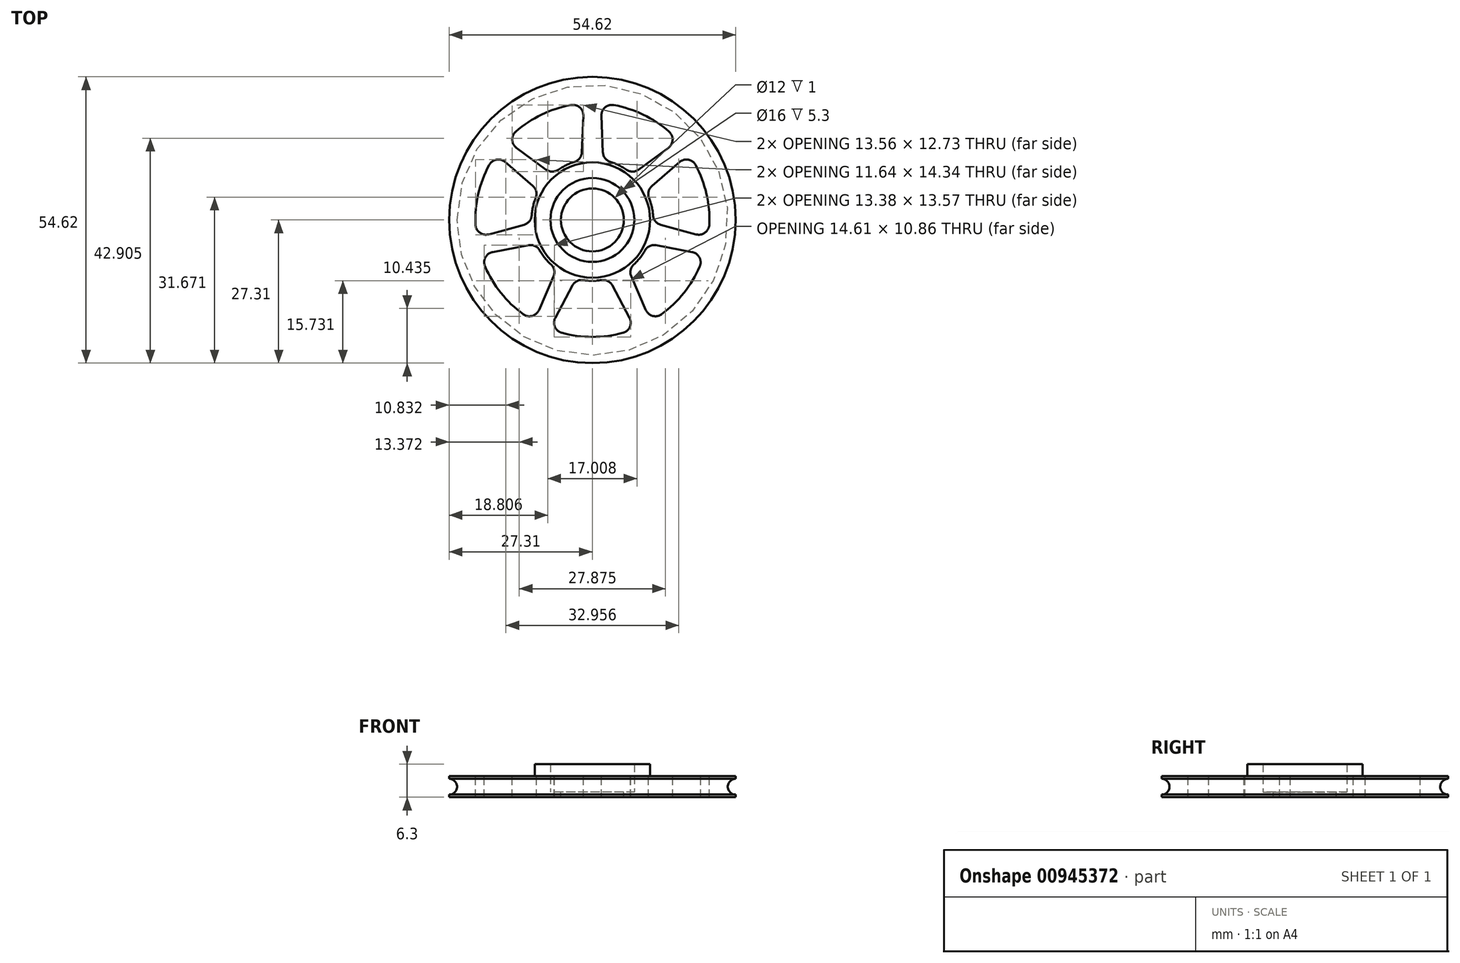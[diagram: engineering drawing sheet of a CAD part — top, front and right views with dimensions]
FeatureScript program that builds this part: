
annotation { "Feature Type Name" : "Feature", "Feature Type Description" : "" }
export const myFeature = defineFeature(function(context is Context, id is Id, definition is map)
    precondition{}
    {
        {
            var Q0;
            Q0=qCreatedBy(makeId("Top.planeOp"),FACE);
            var sketch = newSketch(context, id + "F0", { "sketchPlane" : qUnion([Q0])});
            skCircle(sketch, "E0", {"center": v(0, 0) * mm, "radius": 27.3 * mm});
            skSolve(sketch);
        }
        {
            var Q0;
            Q0=makeQuery(id+"F0.imprint","IMPRINT",FACE,{"disambiguationData":[TD([[makeQuery(id+"F0.imprint","IMPRINT",EDGE,{"derivedFrom":sQuery(id+"F0.wireOp",EDGE,"E0")}),1.0]])]});
            extrude(context, id + "F1", {"entities" : qUnion([Q0]), "depth" : 4 * mm, "offsetDistance" : 25.4 * mm});
        }
        {
            var Q0;
            Q0=makeQuery(id+"F1.opExtrude","CAP_FACE",FACE,{"disambiguationData":[OSD([sQuery(id+"F0.wireOp",EDGE,"E0"),sQuery(id+"F0.wireOp",EDGE,"n39IqKt5-bk1q-LU1x-fgod-8OyBNiFTd7FZ")])],"isStart":false});
            var sketch = newSketch(context, id + "F2", { "sketchPlane" : qUnion([Q0])});
            skCircle(sketch, "E1", {"center": v(0, 0) * mm, "radius": 8 * mm});
            skCircle(sketch, "E2.0", {"center": v(0, 0) * mm, "radius": 11 * mm});
            skSolve(sketch);
        }
        {
            var Q0;
            Q0=qSketchRegion(id+"F2",true);
            extrude(context, id + "F3", {"entities" : qUnion([Q0]), "operationType" : NewBodyOperationType.ADD, "flatOperationType" : FlatOperationType.REMOVE, "depth" : 2.3 * mm, "offsetDistance" : 25.4 * mm, "domain" : OperationDomain.MODEL});
        }
        {
            var Q0;
            Q0=makeQuery(id+"F3.boolean.opBoolean","SPLIT",FACE,{"disambiguationData":[TD([makeQuery(id+"F3.opExtrude","SWEPT_FACE",FACE,{"disambiguationData":[OSD([sQuery(id+"F2.wireOp",EDGE,"E1")])]})])],"derivedFrom":makeQuery(id+"F1.opExtrude","CAP_FACE",FACE,{"disambiguationData":[OSD([sQuery(id+"F0.wireOp",EDGE,"E0")])],"isStart":false})});
            var sketch = newSketch(context, id + "F4", { "sketchPlane" : qUnion([Q0])});
            skCircle(sketch, "E3", {"center": v(0, 0) * mm, "radius": 6 * mm});
            skSolve(sketch);
        }
        {
            var Q0;
            Q0=makeQuery(id+"F4.imprint","IMPRINT",FACE,{"disambiguationData":[TD([[makeQuery(id+"F4.imprint","IMPRINT",EDGE,{"derivedFrom":sQuery(id+"F4.wireOp",EDGE,"E3")}),1.0]])]});
            var Q1;
            Q1=makeQuery(id+"F4.imprint","IMPRINT",FACE,{"disambiguationData":[TD([[makeQuery(id+"F4.imprint","IMPRINT",EDGE,{"derivedFrom":makeQuery(id+"FgYK8jIepfClWtA_1.opExtrude","CAP_EDGE",EDGE,{"disambiguationData":[OSD([sQuery(id+"F8DXjnVyigKkjng_1.wireOp",EDGE,"EUjAMsCd-Zx2B-3j4q-cP5o-T3GrjTijNDqK")])],"isStart":false})}),1.0]])]});
            extrude(context, id + "F5", {"entities" : qUnion([Q0, Q1]), "operationType" : NewBodyOperationType.REMOVE, "oppositeDirection" : true, "depth" : 9 * mm, "offsetDistance" : 25.4 * mm});
        }
        {
            var Q0;
            Q0=qCreatedBy(makeId("Front.planeOp"),FACE);
            var sketch = newSketch(context, id + "F6", { "sketchPlane" : qUnion([Q0])});
            skCircle(sketch, "E4", {"center": v(-27.3, 2) * mm, "radius": 1.5 * mm});
            skLineSegment(sketch, "E5.bottom", {"start": v(-25.8, 0.65) * mm, "end": v(-27.95, 0.65) * mm});
            skLineSegment(sketch, "E5.top", {"start": v(-25.8, 3.35) * mm, "end": v(-27.95, 3.35) * mm});
            skLineSegment(sketch, "E5.left", {"start": v(-25.8, 0.65) * mm, "end": v(-25.8, 3.35) * mm});
            skLineSegment(sketch, "E5.right", {"start": v(-28.8, 1.91) * mm, "end": v(-28.8, 2.09) * mm});
            skLineSegment(sketch, "E6", {"start": v(0, 19.1) * mm, "end": v(0, -12.61) * mm, "construction": true});
            skLineSegment(sketch, "E7", {"start": v(-25.8, 1.83) * mm, "end": v(-25.81, 1.83) * mm});
            skPoint(sketch, "E8.orphan", {"position": v(-38.97, 3.35) * mm});
            skPoint(sketch, "E9.end.orphan", {"position": v(-15.64, 0.65) * mm});
            skPoint(sketch, "E9.start.orphan", {"position": v(-25.8, 2) * mm});
            skSolve(sketch);
        }
        {
            var Q0;
            {var subQ0=sQuery(id+"F6.wireOp",EDGE,"E5.top");var subQ1=sQuery(id+"F6.wireOp",EDGE,"E4");var subQ2=makeQuery(id+"F6.imprint","INTERSECT",VERTEX,{"disambiguationData":[OD(0.0)],"derivedFrom":[subQ1,subQ0]});Q0=makeQuery(id+"F6.imprint","IMPRINT",FACE,{"disambiguationData":[TD([[makeQuery(id+"F6.imprint","IMPRINT",EDGE,{"disambiguationData":[TD([[subQ2,1.0]])],"derivedFrom":subQ1}),1.0]])]});}
            var Q1;
            {var subQ0=sQuery(id+"F6.wireOp",EDGE,"E5.bottom");var subQ1=sQuery(id+"F6.wireOp",EDGE,"E4");var subQ2=makeQuery(id+"F6.imprint","INTERSECT",VERTEX,{"disambiguationData":[OD(0.0)],"derivedFrom":[subQ1,subQ0]});Q1=makeQuery(id+"F6.imprint","IMPRINT",FACE,{"disambiguationData":[TD([[makeQuery(id+"F6.imprint","IMPRINT",EDGE,{"disambiguationData":[TD([[subQ2,-1.0]])],"derivedFrom":subQ1}),1.0]])]});}
            var Q2;
            {var subQ4=sQuery(id+"F6.wireOp",EDGE,"E5.right");Q2=makeQuery(id+"F6.imprint","IMPRINT",FACE,{"disambiguationData":[TD([[makeQuery(id+"F6.imprint","IMPRINT",EDGE,{"derivedFrom":subQ4}),-1.0]])]});}
            var Q3;
            {var subQ0=sQuery(id+"F6.wireOp",EDGE,"p3G3spWP-JurA-dj01-Cwvm-HHlCDoPDIoxd");Q3=makeQuery(id+"F6.imprint","IMPRINT",FACE,{"disambiguationData":[TD([[makeQuery(id+"F6.imprint","IMPRINT",EDGE,{"derivedFrom":subQ0}),1.0]])]});}
            var Q4;
            Q4=makeQuery(id+"F6.imprint","IMPRINT",FACE,{"disambiguationData":[TD([[makeQuery(id+"F6.imprint","IMPRINT",EDGE,{"derivedFrom":sQuery(id+"F6.wireOp",EDGE,"p3G3spWP-JurA-dj01-Cwvm-HHlCDoPDIoxd")}),-1.0]])]});
            var Q5;
            {var subQ0=sQuery(id+"F6.wireOp",EDGE,"E9");Q5=makeQuery(id+"F6.imprint","IMPRINT",FACE,{"disambiguationData":[TD([[makeQuery(id+"F6.imprint","IMPRINT",EDGE,{"derivedFrom":subQ0}),1.0]])]});}
            var Q6;
            Q6=sQuery(id+"F6.wireOp",EDGE,"E6");
            revolve(context, id + "F7", {"operationType" : NewBodyOperationType.REMOVE, "surfaceOperationType" : NewSurfaceOperationType.NEW, "entities" : qUnion([Q0, Q1, Q2, Q3, Q4, Q5]), "axis" : qUnion([Q6]), "revolveType" : RevolveType.FULL, "oppositeDirection" : true});
        }
        {
            var Q0;
            Q0=makeQuery(id+"F3.boolean.opBoolean","SPLIT",FACE,{"disambiguationData":[TD([makeQuery(id+"F3.opExtrude","SWEPT_FACE",FACE,{"disambiguationData":[OSD([sQuery(id+"F2.wireOp",EDGE,"E1")])]})])],"derivedFrom":makeQuery(id+"F1.opExtrude","CAP_FACE",FACE,{"disambiguationData":[OSD([sQuery(id+"F0.wireOp",EDGE,"E0")])],"isStart":false})});
            extrude(context, id + "F8", {"entities" : qUnion([Q0]), "operationType" : NewBodyOperationType.REMOVE, "oppositeDirection" : true, "depth" : 3 * mm, "offsetDistance" : 25 * mm});
        }
        {
            var Q0;
            {var subQ0=sQuery(id+"F0.wireOp",EDGE,"E0");var subQ1=makeQuery(id+"F1.opExtrude","SWEPT_FACE",FACE,{"disambiguationData":[OSD([subQ0])]});Q0=makeQuery(id+"FvaswZWDLJZ7FP9_1.boolean.opBoolean","SPLIT",FACE,{"disambiguationData":[TD([subQ1])],"derivedFrom":makeQuery(id+"F3.boolean.opBoolean","SPLIT",FACE,{"disambiguationData":[TD([subQ1])],"derivedFrom":makeQuery(id+"F1.opExtrude","CAP_FACE",FACE,{"disambiguationData":[OSD([subQ0])],"isStart":false})})});}
            var sketch = newSketch(context, id + "F9", { "sketchPlane" : qUnion([Q0])});
            skArc(sketch, "E10", {"start": v(-4.1, 21.93) * mm, "mid": v(-9.68, 20.1) * mm, "end": v(-14.6, 16.87) * mm});
            skArc(sketch, "E11", {"start": v(-3.41, 11.08) * mm, "mid": v(-5.03, 10.45) * mm, "end": v(-6.54, 9.58) * mm});
            skLineSegment(sketch, "E12.0", {"start": v(-1.73, 19.88) * mm, "end": v(-2, 12.92) * mm});
            skLineSegment(sketch, "E13.0", {"start": v(1.73, 19.88) * mm, "end": v(2, 12.92) * mm});
            skPoint(sketch, "E14.start.orphan", {"position": v(0, 24.6) * mm});
            skPoint(sketch, "E15.visualSharp", {"position": v(-1.63, 22.25) * mm});
            skArc(sketch, "E15.filletArc", {"start": v(-1.73, 19.88) * mm, "mid": v(-2.42, 21.47) * mm, "end": v(-4.1, 21.93) * mm});
            skPoint(sketch, "E16.visualSharp", {"position": v(1.63, 22.25) * mm});
            skArc(sketch, "E16.filletArc", {"start": v(4.1, 21.93) * mm, "mid": v(2.42, 21.47) * mm, "end": v(1.73, 19.88) * mm});
            skPoint(sketch, "E17.visualSharp", {"position": v(-2.06, 11.41) * mm});
            skArc(sketch, "E17.filletArc", {"start": v(-3.41, 11.08) * mm, "mid": v(-2.41, 11.78) * mm, "end": v(-2, 12.92) * mm});
            skPoint(sketch, "E18.visualSharp", {"position": v(2.06, 11.41) * mm});
            skArc(sketch, "E18.filletArc", {"start": v(2, 12.92) * mm, "mid": v(2.41, 11.78) * mm, "end": v(3.41, 11.08) * mm});
            skArc(sketch, "E19.1.0", {"start": v(-16.62, 11.05) * mm, "mid": v(-18.3, 11.5) * mm, "end": v(-19.7, 10.47) * mm});
            skArc(sketch, "E19.1.1", {"start": v(-14.6, 16.87) * mm, "mid": v(-15.28, 15.28) * mm, "end": v(-14.47, 13.75) * mm});
            skLineSegment(sketch, "E19.1.2", {"start": v(-14.47, 13.75) * mm, "end": v(-8.85, 9.62) * mm});
            skLineSegment(sketch, "E19.1.3", {"start": v(-16.62, 11.05) * mm, "end": v(-11.35, 6.49) * mm});
            skArc(sketch, "E19.1.4", {"start": v(-10.8, 4.24) * mm, "mid": v(-10.71, 5.45) * mm, "end": v(-11.35, 6.49) * mm});
            skArc(sketch, "E19.1.5", {"start": v(-8.85, 9.62) * mm, "mid": v(-7.7, 9.23) * mm, "end": v(-6.54, 9.58) * mm});
            skArc(sketch, "E19.2.0", {"start": v(-19, -6.1) * mm, "mid": v(-20.4, -7.13) * mm, "end": v(-20.47, -8.87) * mm});
            skArc(sketch, "E19.2.1", {"start": v(-22.29, -0.89) * mm, "mid": v(-21.47, -2.42) * mm, "end": v(-19.77, -2.74) * mm});
            skLineSegment(sketch, "E19.2.2", {"start": v(-19.77, -2.74) * mm, "end": v(-13.04, -0.92) * mm});
            skLineSegment(sketch, "E19.2.3", {"start": v(-19, -6.1) * mm, "end": v(-12.15, -4.83) * mm});
            skArc(sketch, "E19.2.4", {"start": v(-10.05, -5.8) * mm, "mid": v(-10.94, -4.97) * mm, "end": v(-12.15, -4.83) * mm});
            skArc(sketch, "E19.2.5", {"start": v(-13.04, -0.92) * mm, "mid": v(-12.02, -0.27) * mm, "end": v(-11.57, 0.86) * mm});
            skArc(sketch, "E19.3.0", {"start": v(-7.07, -18.66) * mm, "mid": v(-7.14, -20.4) * mm, "end": v(-5.83, -21.53) * mm});
            skArc(sketch, "E19.3.1", {"start": v(-13.2, -17.98) * mm, "mid": v(-11.5, -18.3) * mm, "end": v(-10.18, -17.16) * mm});
            skLineSegment(sketch, "E19.3.2", {"start": v(-10.18, -17.16) * mm, "end": v(-7.4, -10.77) * mm});
            skLineSegment(sketch, "E19.3.3", {"start": v(-7.07, -18.66) * mm, "end": v(-3.8, -12.5) * mm});
            skArc(sketch, "E19.3.4", {"start": v(-1.74, -11.47) * mm, "mid": v(-2.93, -11.66) * mm, "end": v(-3.8, -12.5) * mm});
            skArc(sketch, "E19.3.5", {"start": v(-7.4, -10.77) * mm, "mid": v(-7.29, -9.56) * mm, "end": v(-7.88, -8.5) * mm});
            skArc(sketch, "E19.4.0", {"start": v(10.18, -17.16) * mm, "mid": v(11.5, -18.3) * mm, "end": v(13.2, -17.98) * mm});
            skArc(sketch, "E19.4.1", {"start": v(5.83, -21.53) * mm, "mid": v(7.14, -20.4) * mm, "end": v(7.07, -18.66) * mm});
            skLineSegment(sketch, "E19.4.2", {"start": v(7.07, -18.66) * mm, "end": v(3.8, -12.5) * mm});
            skLineSegment(sketch, "E19.4.3", {"start": v(10.18, -17.16) * mm, "end": v(7.4, -10.77) * mm});
            skArc(sketch, "E19.4.4", {"start": v(7.88, -8.5) * mm, "mid": v(7.29, -9.56) * mm, "end": v(7.4, -10.77) * mm});
            skArc(sketch, "E19.4.5", {"start": v(3.8, -12.5) * mm, "mid": v(2.93, -11.66) * mm, "end": v(1.74, -11.47) * mm});
            skArc(sketch, "E19.5.0", {"start": v(19.77, -2.74) * mm, "mid": v(21.47, -2.42) * mm, "end": v(22.29, -0.89) * mm});
            skArc(sketch, "E19.5.1", {"start": v(20.47, -8.87) * mm, "mid": v(20.4, -7.13) * mm, "end": v(19, -6.1) * mm});
            skLineSegment(sketch, "E19.5.2", {"start": v(19, -6.1) * mm, "end": v(12.15, -4.83) * mm});
            skLineSegment(sketch, "E19.5.3", {"start": v(19.77, -2.74) * mm, "end": v(13.04, -0.92) * mm});
            skArc(sketch, "E19.5.4", {"start": v(11.57, 0.86) * mm, "mid": v(12.02, -0.27) * mm, "end": v(13.04, -0.92) * mm});
            skArc(sketch, "E19.5.5", {"start": v(12.15, -4.83) * mm, "mid": v(10.94, -4.97) * mm, "end": v(10.05, -5.8) * mm});
            skArc(sketch, "E19.6.0", {"start": v(14.47, 13.75) * mm, "mid": v(15.28, 15.28) * mm, "end": v(14.6, 16.87) * mm});
            skArc(sketch, "E19.6.1", {"start": v(19.7, 10.47) * mm, "mid": v(18.3, 11.5) * mm, "end": v(16.62, 11.05) * mm});
            skLineSegment(sketch, "E19.6.2", {"start": v(16.62, 11.05) * mm, "end": v(11.35, 6.49) * mm});
            skLineSegment(sketch, "E19.6.3", {"start": v(14.47, 13.75) * mm, "end": v(8.85, 9.62) * mm});
            skArc(sketch, "E19.6.4", {"start": v(6.54, 9.58) * mm, "mid": v(7.7, 9.23) * mm, "end": v(8.85, 9.62) * mm});
            skArc(sketch, "E19.6.5", {"start": v(11.35, 6.49) * mm, "mid": v(10.71, 5.45) * mm, "end": v(10.8, 4.24) * mm});
            skArc(sketch, "E20.trimOffspring", {"start": v(-19.7, 10.47) * mm, "mid": v(-21.75, 4.96) * mm, "end": v(-22.29, -0.89) * mm});
            skArc(sketch, "E21.trimOffspring", {"start": v(-10.8, 4.24) * mm, "mid": v(-11.3, 2.58) * mm, "end": v(-11.57, 0.86) * mm});
            skArc(sketch, "E22.trimOffspring", {"start": v(-10.05, -5.8) * mm, "mid": v(-9.07, -7.23) * mm, "end": v(-7.88, -8.5) * mm});
            skArc(sketch, "E23.trimOffspring", {"start": v(-20.47, -8.87) * mm, "mid": v(-17.44, -13.9) * mm, "end": v(-13.2, -17.98) * mm});
            skArc(sketch, "E24.trimOffspring", {"start": v(14.6, 16.87) * mm, "mid": v(9.68, 20.1) * mm, "end": v(4.1, 21.93) * mm});
            skArc(sketch, "E25.trimOffspring", {"start": v(6.54, 9.58) * mm, "mid": v(5.03, 10.45) * mm, "end": v(3.41, 11.08) * mm});
            skArc(sketch, "E26.trimOffspring", {"start": v(11.57, 0.86) * mm, "mid": v(11.3, 2.58) * mm, "end": v(10.8, 4.24) * mm});
            skArc(sketch, "E27.trimOffspring", {"start": v(22.29, -0.89) * mm, "mid": v(21.75, 4.96) * mm, "end": v(19.7, 10.47) * mm});
            skArc(sketch, "E28.trimOffspring", {"start": v(13.2, -17.98) * mm, "mid": v(17.44, -13.9) * mm, "end": v(20.47, -8.87) * mm});
            skArc(sketch, "E29.trimOffspring", {"start": v(7.88, -8.5) * mm, "mid": v(9.07, -7.23) * mm, "end": v(10.05, -5.8) * mm});
            skArc(sketch, "E30.trimOffspring", {"start": v(-1.74, -11.47) * mm, "mid": v(0, -11.6) * mm, "end": v(1.74, -11.47) * mm});
            skArc(sketch, "E31.trimOffspring", {"start": v(-5.83, -21.53) * mm, "mid": v(0, -22.3) * mm, "end": v(5.83, -21.53) * mm});
            skSolve(sketch);
        }
        {
            var Q0;
            Q0 = qSketchRegion(id + "F9", true);
            extrude(context, id + "F10", {"entities" : qUnion([Q0]), "operationType" : NewBodyOperationType.REMOVE, "oppositeDirection" : true, "depth" : 25 * mm, "offsetDistance" : 25 * mm});
        }
    });
